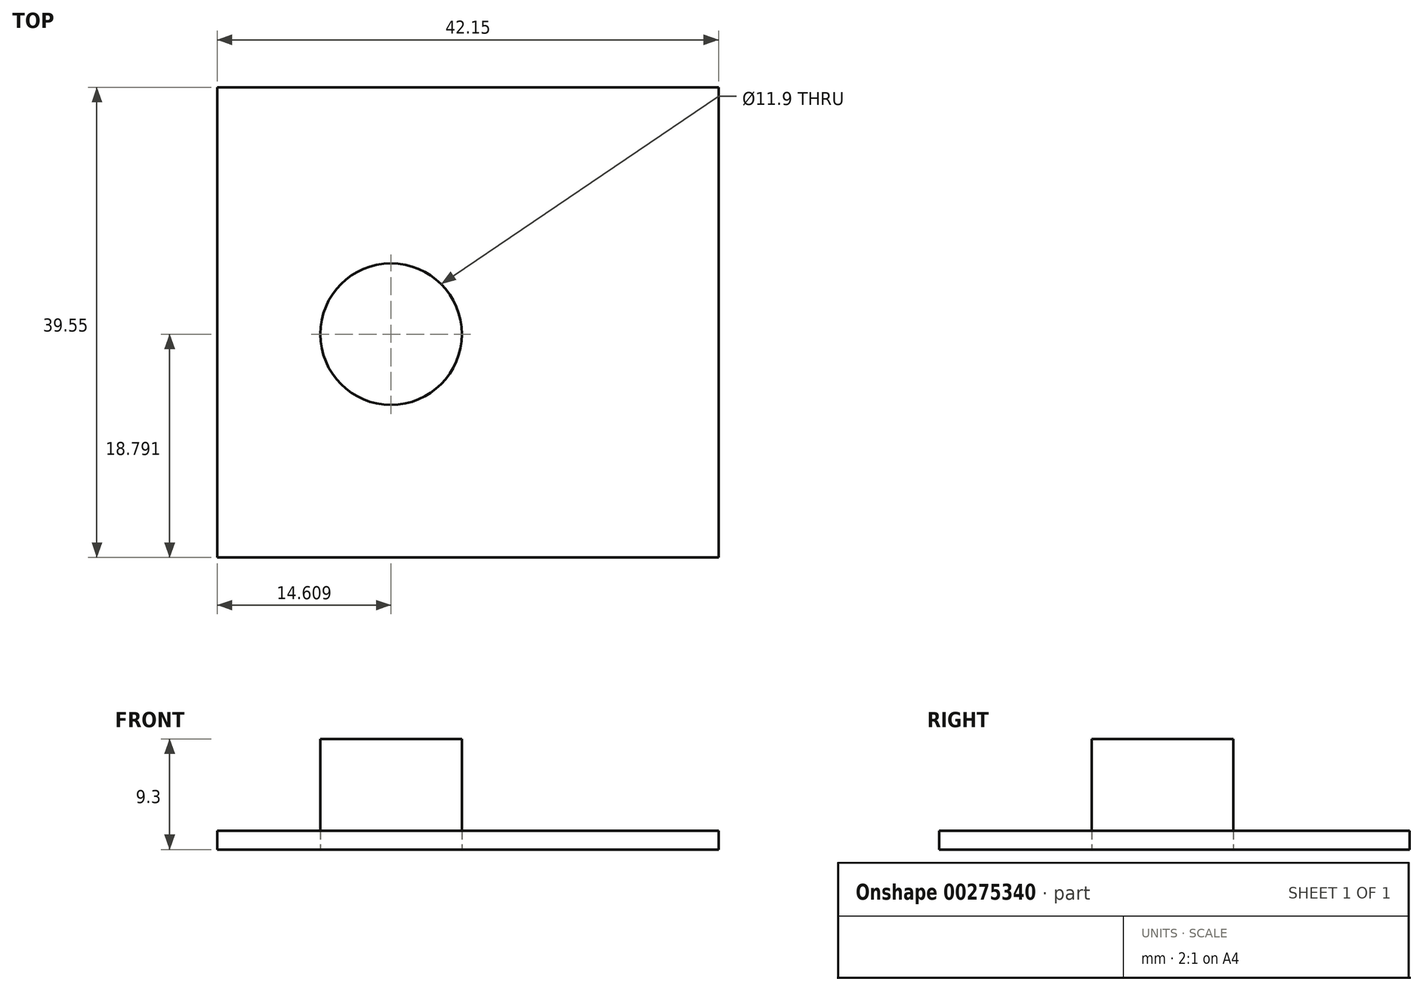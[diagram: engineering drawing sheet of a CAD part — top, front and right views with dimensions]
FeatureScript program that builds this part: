
annotation { "Feature Type Name" : "Feature", "Feature Type Description" : "" }
export const myFeature = defineFeature(function(context is Context, id is Id, definition is map)
    precondition{}
    {
        {
            var Q0;
            Q0=qCreatedBy(makeId("Top.planeOp"),FACE);
            var sketch = newSketch(context, id + "F0", { "sketchPlane" : qUnion([Q0])});
            skLineSegment(sketch, "E0.bottom", {"start": v(0, 0) * mm, "end": v(-42.15, 0) * mm});
            skLineSegment(sketch, "E0.top", {"start": v(0, 39.55) * mm, "end": v(-42.15, 39.55) * mm});
            skLineSegment(sketch, "E0.left", {"start": v(0, 0) * mm, "end": v(0, 39.55) * mm});
            skLineSegment(sketch, "E0.right", {"start": v(-42.15, 0) * mm, "end": v(-42.15, 39.55) * mm});
            skCircle(sketch, "E1", {"center": v(-27.54, 18.8) * mm, "radius": 5.95 * mm});
            skSolve(sketch);
        }
        {
            var Q0;
            Q0=makeQuery(id+"F0.imprint","IMPRINT",FACE,{"disambiguationData":[TD([[makeQuery(id+"F0.imprint","IMPRINT",EDGE,{"derivedFrom":sQuery(id+"F0.wireOp",EDGE,"E1")}),1.0]])]});
            extrude(context, id + "F1", {"entities" : qUnion([Q0]), "depth" : 9.3 * mm});
        }
        {
            var Q0;
            Q0=makeQuery(id+"F0.imprint","IMPRINT",FACE,{"disambiguationData":[TD([[makeQuery(id+"F0.imprint","IMPRINT",EDGE,{"derivedFrom":sQuery(id+"F0.wireOp",EDGE,"E0.bottom")}),-1.0]])]});
            extrude(context, id + "F2", {"entities" : qUnion([Q0]), "depth" : 1.58 * mm});
        }
    });
